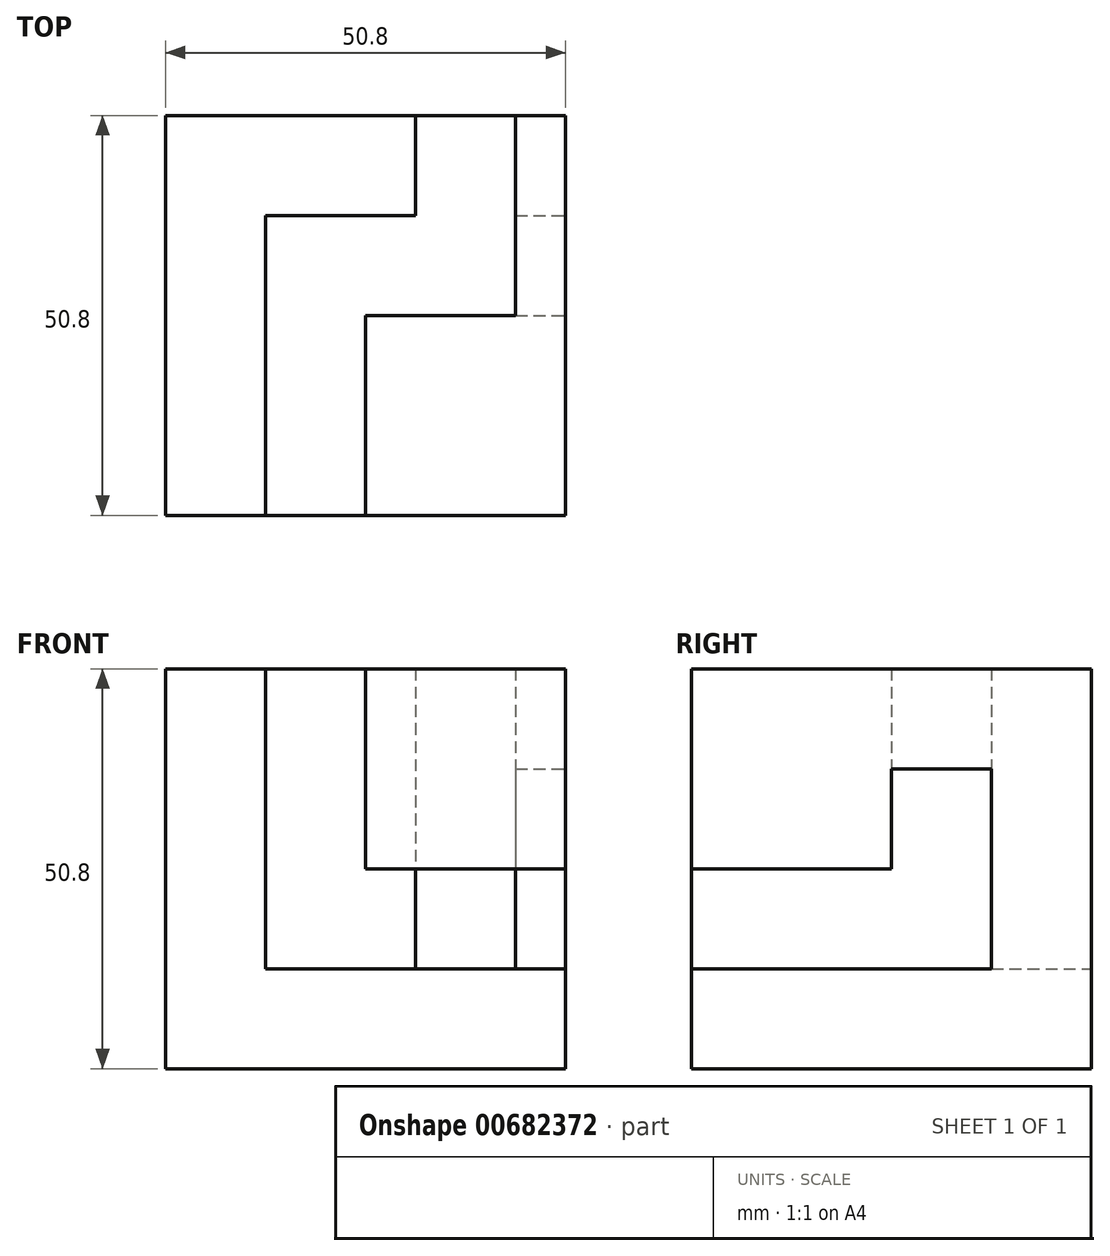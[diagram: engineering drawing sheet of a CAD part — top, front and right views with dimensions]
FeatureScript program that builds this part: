
annotation { "Feature Type Name" : "Feature", "Feature Type Description" : "" }
export const myFeature = defineFeature(function(context is Context, id is Id, definition is map)
    precondition{}
    {
        {
            var Q0;
            Q0=qCreatedBy(makeId("Top.planeOp"),FACE);
            var sketch = newSketch(context, id + "F0", { "sketchPlane" : qUnion([Q0])});
            skLineSegment(sketch, "E0.bottom", {"start": v(0, 0) * mm, "end": v(-50.8, 0) * mm});
            skLineSegment(sketch, "E0.top", {"start": v(0, 50.8) * mm, "end": v(-50.8, 50.8) * mm});
            skLineSegment(sketch, "E0.left", {"start": v(0, 0) * mm, "end": v(0, 50.8) * mm});
            skLineSegment(sketch, "E0.right", {"start": v(-50.8, 0) * mm, "end": v(-50.8, 50.8) * mm});
            skSolve(sketch);
        }
        {
            var Q0;
            Q0=makeQuery(id+"F0.imprint","IMPRINT",FACE,{"disambiguationData":[TD([[makeQuery(id+"F0.imprint","IMPRINT",EDGE,{"derivedFrom":sQuery(id+"F0.wireOp",EDGE,"E0.bottom")}),-1.0]])]});
            extrude(context, id + "F1", {"entities" : qUnion([Q0]), "depth" : 50.8 * mm, "offsetDistance" : 25.4 * mm});
        }
        {
            var Q0;
            Q0=makeQuery(id+"F1.opExtrude","CAP_FACE",FACE,{"disambiguationData":[OSD([sQuery(id+"F0.wireOp",EDGE,"E0.bottom"),sQuery(id+"F0.wireOp",EDGE,"E0.top"),sQuery(id+"F0.wireOp",EDGE,"E0.left"),sQuery(id+"F0.wireOp",EDGE,"E0.right")])],"isStart":false});
            var sketch = newSketch(context, id + "F2", { "sketchPlane" : qUnion([Q0])});
            skLineSegment(sketch, "E1.bottom", {"start": v(0, 0) * mm, "end": v(-38.1, 0) * mm});
            skLineSegment(sketch, "E1.top", {"start": v(0, 38.1) * mm, "end": v(-38.1, 38.1) * mm});
            skLineSegment(sketch, "E1.left", {"start": v(0, 0) * mm, "end": v(0, 38.1) * mm});
            skLineSegment(sketch, "E1.right", {"start": v(-38.1, 0) * mm, "end": v(-38.1, 38.1) * mm});
            skSolve(sketch);
        }
        {
            var Q0;
            Q0=makeQuery(id+"F2.imprint","IMPRINT",FACE,{"disambiguationData":[TD([[makeQuery(id+"F2.imprint","IMPRINT",EDGE,{"derivedFrom":sQuery(id+"F2.wireOp",EDGE,"E1.bottom")}),-1.0]])]});
            extrude(context, id + "F3", {"entities" : qUnion([Q0]), "operationType" : NewBodyOperationType.REMOVE, "oppositeDirection" : true, "depth" : 38.1 * mm, "offsetDistance" : 25.4 * mm});
        }
        {
            var Q0;
            Q0=makeQuery(id+"F1.opExtrude","SWEPT_FACE",FACE,{"disambiguationData":[OSD([sQuery(id+"F0.wireOp",EDGE,"E0.left")])]});
            var sketch = newSketch(context, id + "F4", { "sketchPlane" : qUnion([Q0])});
            skLineSegment(sketch, "E2.bottom", {"start": v(50.8, 50.8) * mm, "end": v(0, 50.8) * mm});
            skLineSegment(sketch, "E2.top", {"start": v(50.8, 38.1) * mm, "end": v(0, 38.1) * mm});
            skLineSegment(sketch, "E2.left", {"start": v(50.8, 50.8) * mm, "end": v(50.8, 38.1) * mm});
            skLineSegment(sketch, "E2.right", {"start": v(0, 50.8) * mm, "end": v(0, 38.1) * mm});
            skSolve(sketch);
        }
        {
            var Q0;
            {var subQ3=sQuery(id+"F4.wireOp",EDGE,"E2.right");Q0=makeQuery(id+"F4.imprint","IMPRINT",FACE,{"disambiguationData":[TD([[makeQuery(id+"F4.imprint","IMPRINT",EDGE,{"derivedFrom":subQ3}),1.0]])]});}
            extrude(context, id + "F5", {"entities" : qUnion([Q0]), "operationType" : NewBodyOperationType.ADD, "oppositeDirection" : true, "depth" : 6.35 * mm, "offsetDistance" : 25.4 * mm});
        }
        {
            var Q0;
            {var subQ0=sQuery(id+"F0.wireOp",EDGE,"E0.left");Q0=makeQuery(id+"F5.boolean.opBoolean","MERGE",FACE,{"derivedFrom":[makeQuery(id+"F1.opExtrude","SWEPT_FACE",FACE,{"disambiguationData":[OSD([subQ0])]}),makeQuery(id+"F5.opExtrude","CAP_FACE",FACE,{"disambiguationData":[OSD([subQ0,sQuery(id+"F2.wireOp",EDGE,"E1.top"),sQuery(id+"F2.wireOp",EDGE,"E1.left"),sQuery(id+"F4.wireOp",EDGE,"E2.bottom"),sQuery(id+"F4.wireOp",EDGE,"E2.top"),sQuery(id+"F4.wireOp",EDGE,"E2.right")])],"isStart":true})]});}
            var sketch = newSketch(context, id + "F6", { "sketchPlane" : qUnion([Q0])});
            skLineSegment(sketch, "E3.bottom", {"start": v(0, 50.8) * mm, "end": v(25.4, 50.8) * mm});
            skLineSegment(sketch, "E3.top", {"start": v(0, 25.4) * mm, "end": v(25.4, 25.4) * mm});
            skLineSegment(sketch, "E3.left", {"start": v(0, 50.8) * mm, "end": v(0, 25.4) * mm});
            skLineSegment(sketch, "E3.right", {"start": v(25.4, 50.8) * mm, "end": v(25.4, 25.4) * mm});
            skSolve(sketch);
        }
        {
            var Q0;
            Q0 = qSketchRegion(id + "F6", true);
            extrude(context, id + "F7", {"entities" : qUnion([Q0]), "operationType" : NewBodyOperationType.ADD, "depth" : -25.4 * mm, "offsetDistance" : 25.4 * mm});
        }
        {
            var Q0;
            Q0=makeQuery(id+"F1.opExtrude","SWEPT_FACE",FACE,{"disambiguationData":[OSD([sQuery(id+"F0.wireOp",EDGE,"E0.top")])]});
            var sketch = newSketch(context, id + "F8", { "sketchPlane" : qUnion([Q0])});
            skLineSegment(sketch, "E4.bottom", {"start": v(0, 0) * mm, "end": v(50.8, 0) * mm});
            skLineSegment(sketch, "E4.top", {"start": v(0, 12.7) * mm, "end": v(50.8, 12.7) * mm});
            skLineSegment(sketch, "E4.left", {"start": v(0, 0) * mm, "end": v(0, 12.7) * mm});
            skLineSegment(sketch, "E4.right", {"start": v(50.8, 0) * mm, "end": v(50.8, 12.7) * mm});
            skLineSegment(sketch, "E5.bottom", {"start": v(0, 50.8) * mm, "end": v(6.35, 50.8) * mm});
            skLineSegment(sketch, "E5.top", {"start": v(0, 12.7) * mm, "end": v(6.35, 12.7) * mm});
            skLineSegment(sketch, "E5.left", {"start": v(0, 50.8) * mm, "end": v(0, 12.7) * mm});
            skLineSegment(sketch, "E5.right", {"start": v(6.35, 50.8) * mm, "end": v(6.35, 12.7) * mm});
            skLineSegment(sketch, "E6.bottom", {"start": v(6.35, 50.8) * mm, "end": v(12.7, 50.8) * mm});
            skLineSegment(sketch, "E6.top", {"start": v(6.35, 12.7) * mm, "end": v(12.7, 12.7) * mm});
            skLineSegment(sketch, "E6.right", {"start": v(12.7, 50.8) * mm, "end": v(12.7, 12.7) * mm});
            skLineSegment(sketch, "E7.bottom", {"start": v(12.7, 50.8) * mm, "end": v(19.05, 50.8) * mm});
            skLineSegment(sketch, "E7.top", {"start": v(12.7, 12.7) * mm, "end": v(19.05, 12.7) * mm});
            skLineSegment(sketch, "E7.right", {"start": v(19.05, 50.8) * mm, "end": v(19.05, 12.7) * mm});
            skSolve(sketch);
        }
        {
            var Q0;
            Q0=makeQuery(id+"F8.imprint","IMPRINT",FACE,{"disambiguationData":[TD([[makeQuery(id+"F8.imprint","IMPRINT",EDGE,{"derivedFrom":sQuery(id+"F8.wireOp",EDGE,"E6.bottom")}),-1.0]])]});
            var Q1;
            Q1=makeQuery(id+"F8.imprint","IMPRINT",FACE,{"disambiguationData":[TD([[makeQuery(id+"F8.imprint","IMPRINT",EDGE,{"derivedFrom":sQuery(id+"F8.wireOp",EDGE,"E7.bottom")}),-1.0]])]});
            extrude(context, id + "F9", {"entities" : qUnion([Q0, Q1]), "operationType" : NewBodyOperationType.REMOVE, "oppositeDirection" : true, "depth" : 12.7 * mm, "offsetDistance" : 25.4 * mm});
        }
    });
